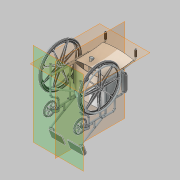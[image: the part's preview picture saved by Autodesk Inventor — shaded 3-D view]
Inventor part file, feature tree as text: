
AUTODESK INVENTOR PART (.ipt)
format: ipt  version: 2021 (Build 250183000, 183)  size: 1,307,136 bytes
history: native  units: mm
features: other x27, plane x4, sketch x1, extrude x1
ambient origin geometry x8: Origin, YZ Plane, XZ Plane, XY Plane, X Axis, Y Axis, Z Axis, Center Point
bodies: Solid1 (feature_tree), Solid2 (feature_tree), Solid3 (feature_tree), Solid4 (feature_tree), Solid5 (feature_tree), Solid6 (feature_tree), Solid7 (feature_tree), Solid8 (feature_tree), Solid9 (feature_tree), Solid10 (feature_tree), Solid11 (feature_tree), Solid12 (feature_tree), Solid13 (feature_tree), Solid14 (feature_tree), Solid15 (feature_tree), Solid16 (feature_tree), Solid17 (feature_tree), Solid18 (feature_tree), Solid19 (feature_tree), Solid20 (feature_tree), Solid21 (feature_tree), Solid22 (feature_tree), Solid23 (feature_tree), Solid24 (feature_tree), Solid25 (feature_tree), Solid26 (feature_tree), Solid27 (feature_tree)
feature tree (33):
  plane  "Work Plane1"
  plane  "Work Plane2"
  sketch  "Sketch1"  dims[d0=215.0mm d1=-440.0mm d9=-890.0mm d17=30.0mm d18=0.0mm d20=50.0mm d25=10.0mm d26=12.217305mm d27=23.911011mm d28=30.0mm d29=30.0mm d30=0.0mm]
  plane  "Work Plane4"
  extrude  "Extrusion3"  [1 undecoded]
  plane  "Work Plane5"
  other  "SideFrame_1:1"
  other  "SideFrame_1:2"
  other  "SideFrame_1:3"
  other  "SideFrame_1:4"
  other  "SideFrame_1:5"
  other  "SideFrame_1:6"
  other  "SideFrame_1:7"
  other  "Arm_2:1"
  other  "Arm_2:2"
  other  "Arm_3:1"
  other  "Arm_3:2"
  other  "ArmPad_4:1"
  other  "ArmPad_5:1"
  other  "Seat_6:1"
  other  "WheelLarge_7:1"
  other  "WheelLarge_7:2"
  other  "WheelLarge_8:1"
  other  "WheelLarge_8:2"
  other  "WheelSmall_16:1"
  other  "CasterFork_17:1"
  other  "WheelSmall_16:2"
  other  "CasterFork_17:2"
  other  "Back_11:1"
  other  "FootRest_12:1"
  other  "FootRest_13:1"
  other  "Grip_14:1"
  other  "Grip_15:1"
note: 1 required parameter value undecoded (feature->parameter linkage not recoverable at this tier; creation-order binding heuristic only, values carry confidence <= 0.55)
